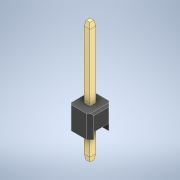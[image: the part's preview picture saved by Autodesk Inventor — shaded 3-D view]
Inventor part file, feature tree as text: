
AUTODESK INVENTOR PART (.ipt)
format: ipt  version: 2021 (Build 250183000, 183)  size: 147,968 bytes
history: native  units: in
note: dims shown in document units (in); Inventor stores cm internally (conversion verified against a paired STEP export)
features: chamfer x1, other x1
ambient origin geometry x8: Origin, YZ Plane, XZ Plane, XY Plane, X Axis, Y Axis, Z Axis, Center Point
bodies: Solid1 (feature_tree), Solid2 (feature_tree)
feature tree (2):
  chamfer  "Chamfer3"  [1 undecoded]
  other  "Boss-Extrude3"
note: 1 required parameter value undecoded (feature->parameter linkage not recoverable at this tier; creation-order binding heuristic only, values carry confidence <= 0.55)
